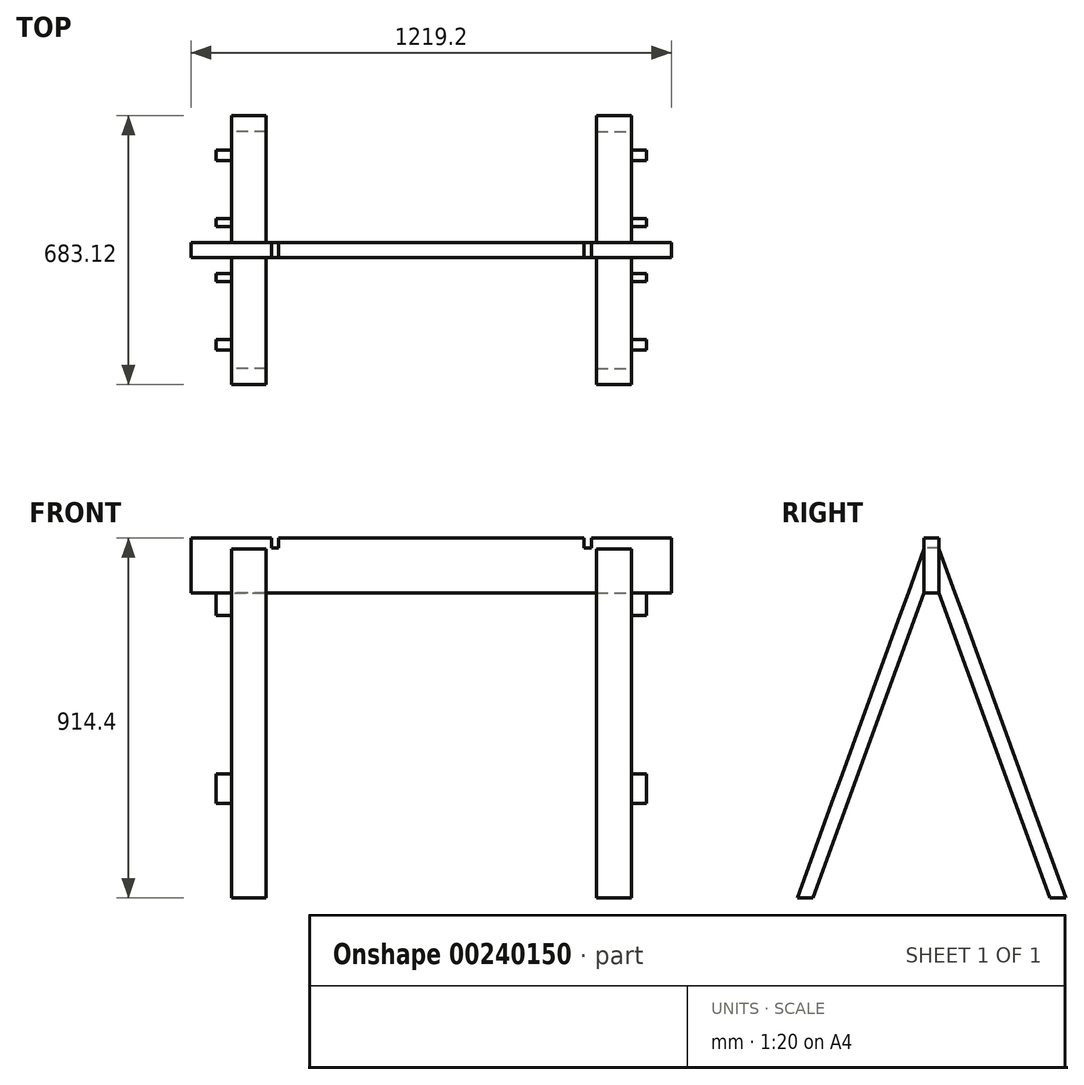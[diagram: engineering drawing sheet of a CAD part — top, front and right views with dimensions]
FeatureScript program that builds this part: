
annotation { "Feature Type Name" : "Feature", "Feature Type Description" : "" }
export const myFeature = defineFeature(function(context is Context, id is Id, definition is map)
    precondition{}
    {
        {
            var Q0;
            Q0=qCreatedBy(makeId("Top.planeOp"),FACE);
            var sketch = newSketch(context, id + "F0", { "sketchPlane" : qUnion([Q0])});
            skLineSegment(sketch, "E0", {"start": v(-609.6, 0) * mm, "end": v(-609.6, 19.05) * mm});
            skLineSegment(sketch, "E1", {"start": v(-609.6, 19.05) * mm, "end": v(609.6, 19.05) * mm});
            skLineSegment(sketch, "E2", {"start": v(609.6, 19.05) * mm, "end": v(609.6, 0) * mm});
            skLineSegment(sketch, "E3.MirrorCS", {"start": v(609.6, -19.05) * mm, "end": v(609.6, 0) * mm});
            skLineSegment(sketch, "E4.MirrorCS", {"start": v(-609.6, 0) * mm, "end": v(-609.6, -19.05) * mm});
            skLineSegment(sketch, "E5", {"start": v(-609.6, -19.05) * mm, "end": v(609.6, -19.05) * mm});
            skSolve(sketch);
        }
        {
            var Q0;
            Q0 = qSketchRegion(id + "F0", true);
            extrude(context, id + "F1", {"entities" : qUnion([Q0]), "endBound" : BoundingType.SYMMETRIC, "depth" : 139.7 * mm});
        }
        {
            var Q0;
            Q0=makeQuery(id+"F1.opExtrude","SWEPT_FACE",FACE,{"disambiguationData":[OSD([sQuery(id+"F0.wireOp",EDGE,"E0"),sQuery(id+"F0.wireOp",EDGE,"E4.MirrorCS")])]});
            cPlane(context, id + "F2", {"entities" : qUnion([Q0]), "cplaneType" : CPlaneType.OFFSET, "offset" : 101.6 * mm, "oppositeDirection" : true, "width" : 152.4 * mm, "height" : 152.4 * mm});
        }
        {
            var Q0;
            Q0=qCreatedBy(id+"F2.planeOp",FACE);
            var sketch = newSketch(context, id + "F3", { "sketchPlane" : qUnion([Q0])});
            skLineSegment(sketch, "E6.0", {"start": v(19.05, 69.85) * mm, "end": v(19.05, -69.85) * mm});
            skPoint(sketch, "E7.0", {"position": v(0, 69.85) * mm});
            skLineSegment(sketch, "E8.0.0", {"start": v(-19.05, -69.85) * mm, "end": v(19.05, -69.85) * mm});
            skLineSegment(sketch, "E8.0.1", {"start": v(19.05, -69.85) * mm, "end": v(19.05, 69.85) * mm});
            skLineSegment(sketch, "E8.0.2", {"start": v(19.05, 69.85) * mm, "end": v(-19.05, 69.85) * mm});
            skLineSegment(sketch, "E8.0.3", {"start": v(-19.05, 69.85) * mm, "end": v(-19.05, -69.85) * mm});
            skLineSegment(sketch, "E9", {"start": v(0, 69.85) * mm, "end": v(0, -844.55) * mm, "construction": true});
            skLineSegment(sketch, "E10", {"start": v(19.05, -69.85) * mm, "end": v(301.02, -844.55) * mm});
            skLineSegment(sketch, "E11", {"start": v(19.05, -69.85) * mm, "end": v(19.05, -123.83) * mm, "construction": true});
            skLineSegment(sketch, "E12", {"start": v(19.05, -69.85) * mm, "end": v(-0.71, -77.04) * mm, "construction": true});
            skLineSegment(sketch, "E13", {"start": v(0, -844.55) * mm, "end": v(811.33, -844.55) * mm, "construction": true});
            skLineSegment(sketch, "E14.0", {"start": v(19.05, 41.55) * mm, "end": v(341.56, -844.55) * mm});
            skLineSegment(sketch, "E15", {"start": v(19.05, 41.55) * mm, "end": v(19.05, -69.85) * mm});
            skLineSegment(sketch, "E16", {"start": v(301.02, -844.55) * mm, "end": v(341.56, -844.55) * mm});
            skLineSegment(sketch, "E17", {"start": v(341.56, -844.55) * mm, "end": v(290.16, -863.26) * mm, "construction": true});
            skSolve(sketch);
        }
        {
            var Q0;
            Q0=makeQuery(id+"F1.opExtrude","SWEPT_FACE",FACE,{"disambiguationData":[OSD([sQuery(id+"F0.wireOp",EDGE,"E5")])]});
            var sketch = newSketch(context, id + "F4", { "sketchPlane" : qUnion([Q0])});
            skLineSegment(sketch, "E18", {"start": v(-609.6, 69.85) * mm, "end": v(-406.4, 69.85) * mm, "construction": true});
            skLineSegment(sketch, "E19", {"start": v(-406.4, 69.85) * mm, "end": v(-406.4, 44.45) * mm});
            skLineSegment(sketch, "E20", {"start": v(-406.4, 44.45) * mm, "end": v(-387.35, 44.45) * mm});
            skLineSegment(sketch, "E21", {"start": v(-387.35, 44.45) * mm, "end": v(-387.35, 69.85) * mm});
            skLineSegment(sketch, "E22", {"start": v(-387.35, 69.85) * mm, "end": v(-406.4, 69.85) * mm});
            skLineSegment(sketch, "E23.MirrorCS", {"start": v(609.6, 69.85) * mm, "end": v(406.4, 69.85) * mm, "construction": true});
            skLineSegment(sketch, "E24.MirrorCS", {"start": v(406.4, 69.85) * mm, "end": v(406.4, 44.45) * mm});
            skLineSegment(sketch, "E25.MirrorCS", {"start": v(387.35, 44.45) * mm, "end": v(387.35, 69.85) * mm});
            skLineSegment(sketch, "E26.MirrorCS", {"start": v(406.4, 44.45) * mm, "end": v(387.35, 44.45) * mm});
            skLineSegment(sketch, "E27.MirrorCS", {"start": v(387.35, 69.85) * mm, "end": v(406.4, 69.85) * mm});
            skSolve(sketch);
        }
        {
            var Q0;
            Q0 = qSketchRegion(id + "F4", true);
            extrude(context, id + "F5", {"entities" : qUnion([Q0]), "operationType" : NewBodyOperationType.REMOVE, "oppositeDirection" : true, "depth" : 50.8 * mm});
        }
        {
            var Q0;
            Q0=makeQuery(id+"F3.imprint","IMPRINT",FACE,{"disambiguationData":[TD([[makeQuery(id+"F3.imprint","IMPRINT",EDGE,{"derivedFrom":sQuery(id+"F3.wireOp",EDGE,"E10")}),1.0]])]});
            extrude(context, id + "F6", {"entities" : qUnion([Q0]), "oppositeDirection" : true, "depth" : 88.9 * mm});
        }
        {
            var Q0;
            Q0=makeQuery(id+"F6.opExtrude","SWEPT_BODY",BODY,{"disambiguationData":[OSD([sQuery(id+"F3.wireOp",EDGE,"E10"),sQuery(id+"F3.wireOp",EDGE,"E14.0"),sQuery(id+"F3.wireOp",EDGE,"E15"),sQuery(id+"F3.wireOp",EDGE,"E16")])]});
            var Q1;
            Q1=qCreatedBy(makeId("Front.planeOp"),FACE);
            mirror(context, id + "F7", {"entities" : qUnion([Q0]), "mirrorPlane" : qUnion([Q1])});
        }
        {
            var Q0;
            Q0=makeQuery(id+"F7.opPattern","COPY",FACE,{"derivedFrom":makeQuery(id+"F6.opExtrude","CAP_FACE",FACE,{"disambiguationData":[OSD([sQuery(id+"F3.wireOp",EDGE,"E10"),sQuery(id+"F3.wireOp",EDGE,"E14.0"),sQuery(id+"F3.wireOp",EDGE,"E15"),sQuery(id+"F3.wireOp",EDGE,"E16")])],"isStart":true}),"instanceName":"1"});
            var sketch = newSketch(context, id + "F8", { "sketchPlane" : qUnion([Q0])});
            skPoint(sketch, "E28.0", {"position": v(0, 69.85) * mm});
            skLineSegment(sketch, "E29", {"start": v(0, 69.85) * mm, "end": v(0, -844.55) * mm, "construction": true});
            skLineSegment(sketch, "E30", {"start": v(0, -611.6) * mm, "end": v(254, -611.6) * mm, "construction": true});
            skLineSegment(sketch, "E31", {"start": v(254, -611.6) * mm, "end": v(254, -565.27) * mm, "construction": true});
            skLineSegment(sketch, "E32.0", {"start": v(-19.05, 41.55) * mm, "end": v(-341.56, -844.55) * mm});
            skLineSegment(sketch, "E33.0", {"start": v(19.05, 41.55) * mm, "end": v(341.56, -844.55) * mm});
            skLineSegment(sketch, "E34", {"start": v(254, -603.97) * mm, "end": v(-254, -603.97) * mm});
            skLineSegment(sketch, "E35.0", {"start": v(221.64, -515.07) * mm, "end": v(-221.64, -515.07) * mm});
            skLineSegment(sketch, "E36", {"start": v(-221.64, -515.07) * mm, "end": v(-254, -603.97) * mm});
            skLineSegment(sketch, "E37", {"start": v(254, -603.97) * mm, "end": v(221.64, -515.07) * mm});
            skLineSegment(sketch, "E38.0", {"start": v(-19.05, -69.85) * mm, "end": v(19.05, -69.85) * mm});
            skLineSegment(sketch, "E39", {"start": v(59.6, -69.85) * mm, "end": v(-59.6, -69.85) * mm});
            skPoint(sketch, "E39.endSnap0", {"position": v(0, -69.85) * mm});
            skLineSegment(sketch, "E40.0", {"start": v(91.95, -158.75) * mm, "end": v(-91.95, -158.75) * mm});
            skLineSegment(sketch, "E41", {"start": v(-59.6, -69.85) * mm, "end": v(-91.95, -158.75) * mm});
            skLineSegment(sketch, "E42", {"start": v(59.6, -69.85) * mm, "end": v(91.95, -158.75) * mm});
            skLineSegment(sketch, "E43", {"start": v(91.95, -158.75) * mm, "end": v(91.95, -69.85) * mm, "construction": true});
            skSolve(sketch);
        }
        {
            var Q0;
            {var subQ3=sQuery(id+"F8.wireOp",EDGE,"E41");Q0=makeQuery(id+"F8.imprint","IMPRINT",FACE,{"disambiguationData":[TD([[makeQuery(id+"F8.imprint","IMPRINT",EDGE,{"derivedFrom":subQ3}),1.0]])]});}
            var Q1;
            {var subQ3=sQuery(id+"F8.wireOp",EDGE,"E42");Q1=makeQuery(id+"F8.imprint","IMPRINT",FACE,{"disambiguationData":[TD([[makeQuery(id+"F8.imprint","IMPRINT",EDGE,{"derivedFrom":subQ3}),-1.0]])]});}
            extrude(context, id + "F9", {"entities" : qUnion([Q0, Q1]), "depth" : 38.1 * mm});
        }
        {
            var Q0;
            {var subQ0=sQuery(id+"F8.wireOp",EDGE,"E37");Q0=makeQuery(id+"F8.imprint","IMPRINT",FACE,{"disambiguationData":[TD([[makeQuery(id+"F8.imprint","IMPRINT",EDGE,{"derivedFrom":subQ0}),1.0]])]});}
            var Q1;
            {var subQ0=sQuery(id+"F8.wireOp",EDGE,"E36");Q1=makeQuery(id+"F8.imprint","IMPRINT",FACE,{"disambiguationData":[TD([[makeQuery(id+"F8.imprint","IMPRINT",EDGE,{"derivedFrom":subQ0}),1.0]])]});}
            extrude(context, id + "F10", {"entities" : qUnion([Q0, Q1]), "depth" : 38.1 * mm});
        }
        {
            var Q0;
            Q0=makeQuery(id+"F7.opPattern","COPY",BODY,{"derivedFrom":makeQuery(id+"F6.opExtrude","SWEPT_BODY",BODY,{"disambiguationData":[OSD([sQuery(id+"F3.wireOp",EDGE,"E10"),sQuery(id+"F3.wireOp",EDGE,"E14.0"),sQuery(id+"F3.wireOp",EDGE,"E15"),sQuery(id+"F3.wireOp",EDGE,"E16")])]}),"instanceName":"1"});
            var Q1;
            Q1=makeQuery(id+"F9.opExtrude","SWEPT_BODY",BODY,{"disambiguationData":[OSD([sQuery(id+"F8.wireOp",EDGE,"E39"),sQuery(id+"F8.wireOp",EDGE,"E40.0"),sQuery(id+"F8.wireOp",EDGE,"E41"),sQuery(id+"F8.wireOp",EDGE,"E42")])]});
            var Q2;
            Q2=makeQuery(id+"F6.opExtrude","SWEPT_BODY",BODY,{"disambiguationData":[OSD([sQuery(id+"F3.wireOp",EDGE,"E10"),sQuery(id+"F3.wireOp",EDGE,"E14.0"),sQuery(id+"F3.wireOp",EDGE,"E15"),sQuery(id+"F3.wireOp",EDGE,"E16")])]});
            var Q3;
            Q3=makeQuery(id+"F10.opExtrude","SWEPT_BODY",BODY,{"disambiguationData":[OSD([sQuery(id+"F8.wireOp",EDGE,"E34"),sQuery(id+"F8.wireOp",EDGE,"E35.0"),sQuery(id+"F8.wireOp",EDGE,"E36"),sQuery(id+"F8.wireOp",EDGE,"E37")])]});
            var Q4;
            Q4=qCreatedBy(makeId("Right.planeOp"),FACE);
            mirror(context, id + "F11", {"entities" : qUnion([Q0, Q1, Q2, Q3]), "mirrorPlane" : qUnion([Q4])});
        }
    });
